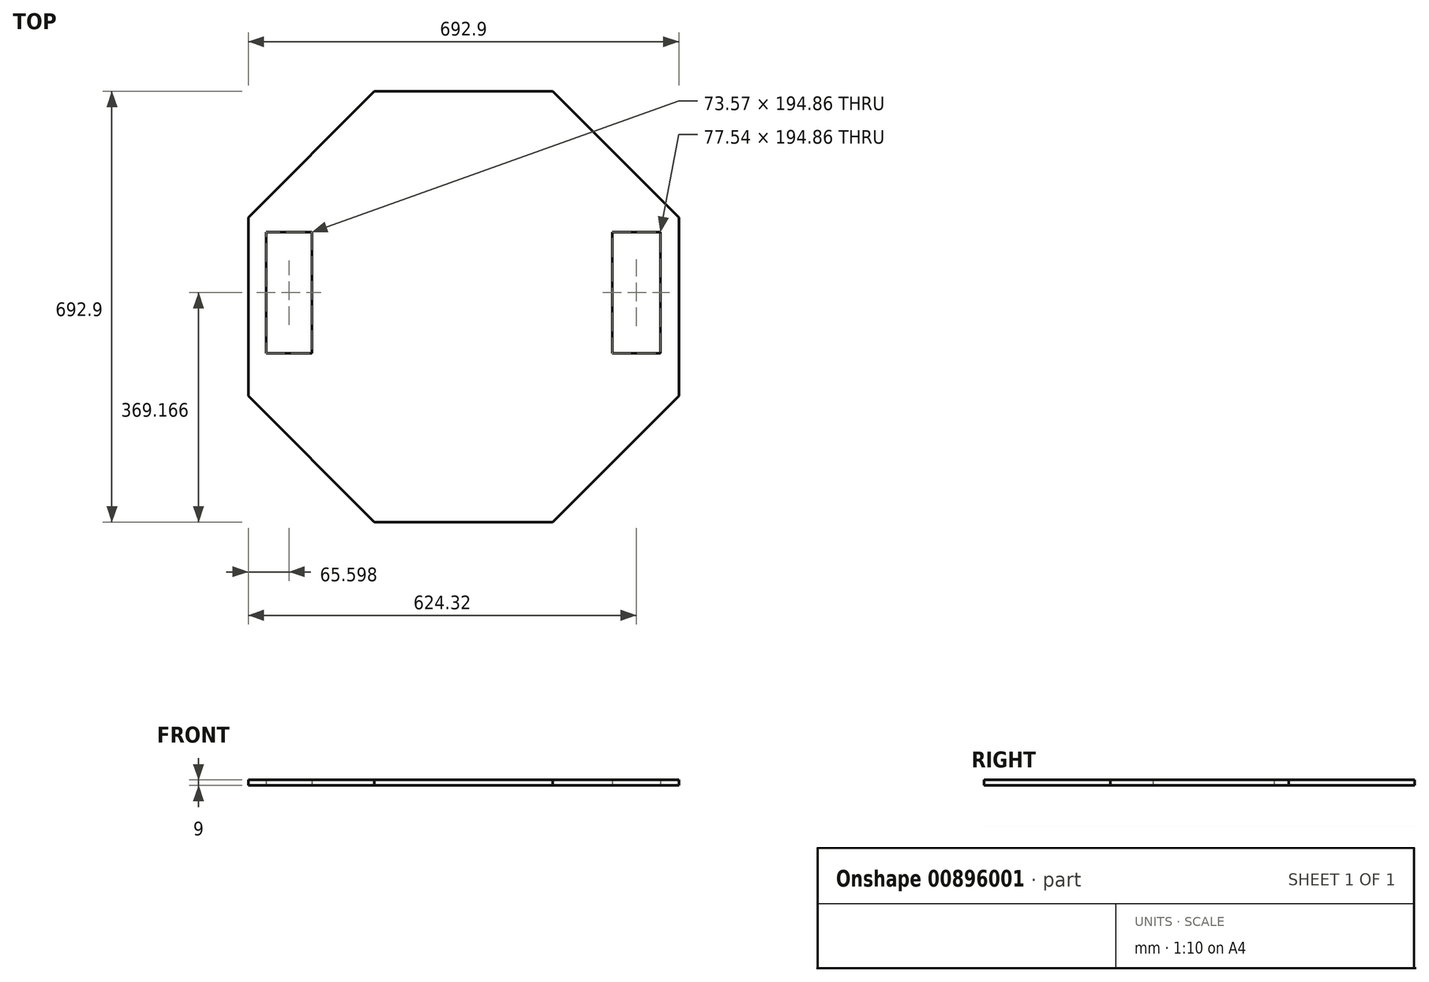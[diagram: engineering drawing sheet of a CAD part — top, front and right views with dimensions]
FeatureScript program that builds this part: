
annotation { "Feature Type Name" : "Feature", "Feature Type Description" : "" }
export const myFeature = defineFeature(function(context is Context, id is Id, definition is map)
    precondition{}
    {
        {
            var Q0;
            Q0=qCreatedBy(makeId("Top.planeOp"),FACE);
            var sketch = newSketch(context, id + "F0", { "sketchPlane" : qUnion([Q0])});
            skCircle(sketch, "E0.cCircle", {"center": v(0, 0) * mm, "radius": 375 * mm, "construction": true});
            skLineSegment(sketch, "E0.0", {"start": v(-143.5, 346.45) * mm, "end": v(143.5, 346.45) * mm});
            skLineSegment(sketch, "E0.1", {"start": v(143.5, 346.45) * mm, "end": v(346.45, 143.5) * mm});
            skLineSegment(sketch, "E0.2", {"start": v(346.45, 143.5) * mm, "end": v(346.45, -143.5) * mm});
            skLineSegment(sketch, "E0.3", {"start": v(346.45, -143.5) * mm, "end": v(143.5, -346.45) * mm});
            skLineSegment(sketch, "E0.4", {"start": v(143.5, -346.45) * mm, "end": v(-143.5, -346.45) * mm});
            skLineSegment(sketch, "E0.5", {"start": v(-143.5, -346.45) * mm, "end": v(-346.45, -143.5) * mm});
            skLineSegment(sketch, "E0.6", {"start": v(-346.45, -143.5) * mm, "end": v(-346.45, 143.5) * mm});
            skLineSegment(sketch, "E0.7", {"start": v(-346.45, 143.5) * mm, "end": v(-143.5, 346.45) * mm});
            skSolve(sketch);
        }
        {
            var Q0;
            Q0=makeQuery(id+"F0.imprint","IMPRINT",FACE,{"disambiguationData":[TD([[makeQuery(id+"F0.imprint","IMPRINT",EDGE,{"derivedFrom":sQuery(id+"F0.wireOp",EDGE,"E0.0")}),-1.0]])]});
            extrude(context, id + "F1", {"entities" : qUnion([Q0]), "depth" : 9 * mm, "offsetDistance" : 25.4 * mm});
        }
        {
            var Q0;
            Q0=makeQuery(id+"F0.imprint","IMPRINT",FACE,{"disambiguationData":[TD([[makeQuery(id+"F0.imprint","IMPRINT",EDGE,{"derivedFrom":sQuery(id+"F0.wireOp",EDGE,"E0.0")}),-1.0]])]});
            var sketch = newSketch(context, id + "F2", { "sketchPlane" : qUnion([Q0])});
            skLineSegment(sketch, "E1.bottom", {"start": v(-317.64, -74.71) * mm, "end": v(-244.07, -74.71) * mm});
            skLineSegment(sketch, "E1.top", {"start": v(-317.64, 120.14) * mm, "end": v(-244.07, 120.14) * mm});
            skLineSegment(sketch, "E1.left", {"start": v(-317.64, -74.71) * mm, "end": v(-317.64, 120.14) * mm});
            skLineSegment(sketch, "E1.right", {"start": v(-244.07, -74.71) * mm, "end": v(-244.07, 120.14) * mm});
            skLineSegment(sketch, "E2.bottom", {"start": v(239.1, -74.71) * mm, "end": v(316.64, -74.71) * mm});
            skLineSegment(sketch, "E2.top", {"start": v(239.1, 120.14) * mm, "end": v(316.64, 120.14) * mm});
            skLineSegment(sketch, "E2.left", {"start": v(239.1, -74.71) * mm, "end": v(239.1, 120.14) * mm});
            skLineSegment(sketch, "E2.right", {"start": v(316.64, -74.71) * mm, "end": v(316.64, 120.14) * mm});
            skSolve(sketch);
        }
        {
            var Q0;
            Q0=makeQuery(id+"F2.imprint","IMPRINT",FACE,{"disambiguationData":[TD([[makeQuery(id+"F2.imprint","IMPRINT",EDGE,{"derivedFrom":sQuery(id+"F2.wireOp",EDGE,"E2.bottom")}),1.0]])]});
            extrude(context, id + "F3", {"entities" : qUnion([Q0]), "operationType" : NewBodyOperationType.REMOVE, "endBound" : BoundingType.THROUGH_ALL, "depth" : 25 * mm, "offsetDistance" : 25 * mm});
        }
        {
            var Q0;
            Q0=makeQuery(id+"F2.imprint","IMPRINT",FACE,{"disambiguationData":[TD([[makeQuery(id+"F2.imprint","IMPRINT",EDGE,{"derivedFrom":sQuery(id+"F2.wireOp",EDGE,"E1.bottom")}),1.0]])]});
            extrude(context, id + "F4", {"entities" : qUnion([Q0]), "operationType" : NewBodyOperationType.REMOVE, "endBound" : BoundingType.THROUGH_ALL, "depth" : 25 * mm, "offsetDistance" : 25 * mm});
        }
    });
